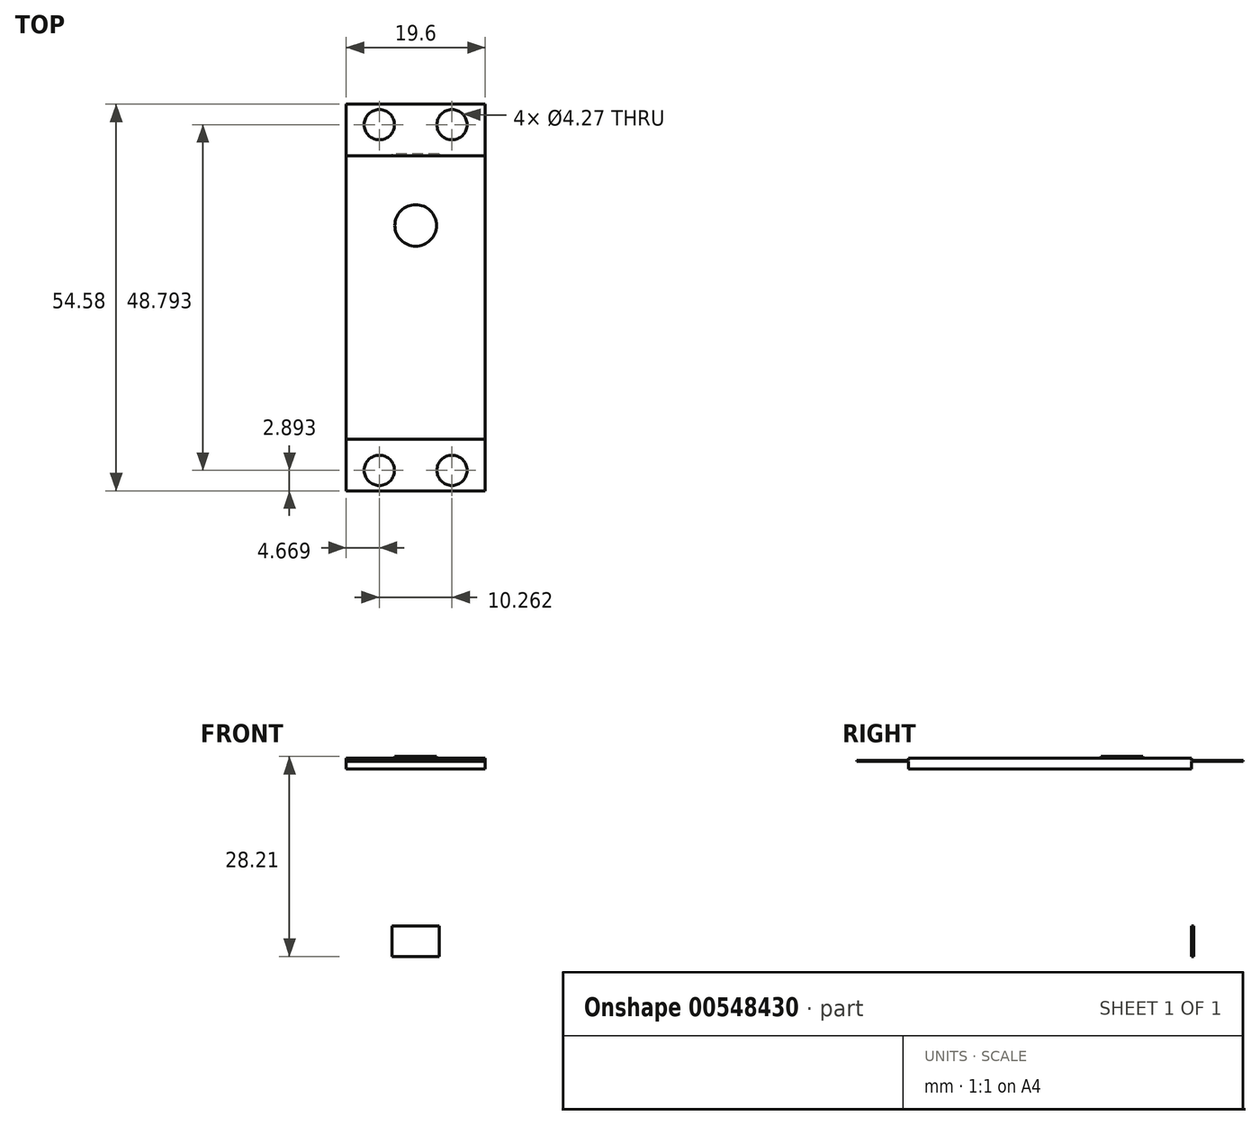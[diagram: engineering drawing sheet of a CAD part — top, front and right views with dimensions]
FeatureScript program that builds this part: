
annotation { "Feature Type Name" : "Feature", "Feature Type Description" : "" }
export const myFeature = defineFeature(function(context is Context, id is Id, definition is map)
    precondition{}
    {
        {
            assignVariable(context, id + "F0", {"name" : "EarDepth", "anyValue" : .3250});
        }
        {
            assignVariable(context, id + "F1", {"name" : "EarThick", "anyValue" : .137});
        }
        {
            assignVariable(context, id + "F2", {"name" : "ServoL", "anyValue" : 1.54});
        }
        {
            assignVariable(context, id + "F3", {"name" : "ServoAxleL", "anyValue" : 0.23});
        }
        {
            var Q0;
            Q0=qCreatedBy(makeId("Top.planeOp"),FACE);
            var sketch = newSketch(context, id + "F4", { "sketchPlane" : qUnion([Q0])});
            skLineSegment(sketch, "E0.bottom", {"start": v(-9.8, -27.3) * mm, "end": v(9.8, -27.3) * mm});
            skLineSegment(sketch, "E0.top", {"start": v(-9.8, 27.3) * mm, "end": v(9.8, 27.3) * mm});
            skLineSegment(sketch, "E0.left", {"start": v(-9.8, -27.3) * mm, "end": v(-9.8, 27.3) * mm});
            skLineSegment(sketch, "E0.right", {"start": v(9.8, -27.3) * mm, "end": v(9.8, 27.3) * mm});
            skPoint(sketch, "E0.middle", {"position": v(0, 0) * mm});
            skLineSegment(sketch, "E1", {"start": v(-9.8, 19.98) * mm, "end": v(9.8, 19.98) * mm});
            skLineSegment(sketch, "E2", {"start": v(-9.8, -19.98) * mm, "end": v(9.8, -19.98) * mm});
            skCircle(sketch, "E3", {"center": v(0, 10.17) * mm, "radius": 2.93 * mm});
            skCircle(sketch, "E4", {"center": v(5.13, 24.4) * mm, "radius": 2.13 * mm});
            skCircle(sketch, "E5.MirrorC", {"center": v(-5.13, 24.4) * mm, "radius": 2.13 * mm});
            skCircle(sketch, "E6.MirrorC", {"center": v(-5.13, -24.4) * mm, "radius": 2.13 * mm});
            skCircle(sketch, "E7.MirrorC", {"center": v(5.13, -24.4) * mm, "radius": 2.13 * mm});
            skSolve(sketch);
        }
        {
            var Q0;
            Q0=makeQuery(id+"F4.imprint","IMPRINT",FACE,{"disambiguationData":[TD([[makeQuery(id+"F4.imprint","IMPRINT",EDGE,{"derivedFrom":sQuery(id+"F4.wireOp",EDGE,"E3")}),1.0]])]});
            extrude(context, id + "F5", {"entities" : qUnion([Q0]), "depth" : (getVariable(context, 'ServoAxleL') + getVariable(context, 'EarDepth')) * mm, "offsetDistance" : 25.4 * mm});
        }
        {
            var Q0;
            {var subQ1=sQuery(id+"F4.wireOp",EDGE,"E1");Q0=makeQuery(id+"F4.imprint","IMPRINT",FACE,{"disambiguationData":[TD([[makeQuery(id+"F4.imprint","IMPRINT",EDGE,{"derivedFrom":subQ1}),-1.0]])]});}
            var Q1;
            Q1=makeQuery(id+"F4.imprint","IMPRINT",FACE,{"disambiguationData":[TD([[makeQuery(id+"F4.imprint","IMPRINT",EDGE,{"derivedFrom":sQuery(id+"F4.wireOp",EDGE,"E3")}),1.0]])]});
            extrude(context, id + "F6", {"entities" : qUnion([Q0, Q1]), "operationType" : NewBodyOperationType.ADD, "depth" : (getVariable(context, 'EarDepth')) * mm, "offsetDistance" : 25.4 * mm, "hasSecondDirection" : true, "secondDirectionOppositeDirection" : true, "secondDirectionDepth" : (getVariable(context, 'ServoL') - getVariable(context, 'EarDepth')) * mm});
        }
        {
            var Q0;
            {var subQ2=sQuery(id+"F4.wireOp",EDGE,"E0.top");Q0=makeQuery(id+"F4.imprint","IMPRINT",FACE,{"disambiguationData":[TD([[makeQuery(id+"F4.imprint","IMPRINT",EDGE,{"derivedFrom":subQ2}),-1.0]])]});}
            var Q1;
            {var subQ2=sQuery(id+"F4.wireOp",EDGE,"E0.bottom");Q1=makeQuery(id+"F4.imprint","IMPRINT",FACE,{"disambiguationData":[TD([[makeQuery(id+"F4.imprint","IMPRINT",EDGE,{"derivedFrom":subQ2}),1.0]])]});}
            extrude(context, id + "F7", {"entities" : qUnion([Q0, Q1]), "operationType" : NewBodyOperationType.ADD, "oppositeDirection" : true, "depth" : (getVariable(context, 'EarThick')) * mm, "offsetDistance" : 25.4 * mm});
        }
        {
            assignVariable(context, id + "F8", {"name" : "WireH", "anyValue" : .3});
        }
        {
            var Q0;
            {var subQ0=sQuery(id+"F4.wireOp",EDGE,"E1");var subQ1=sQuery(id+"F4.wireOp",EDGE,"E0.right");var subQ2=sQuery(id+"F4.wireOp",EDGE,"E0.left");var subQ5=sQuery(id+"F4.wireOp",EDGE,"E2");Q0=makeQuery(id+"F7.boolean.opBoolean","SPLIT",FACE,{"disambiguationData":[TD([makeQuery(id+"F6.opExtrude","CAP_FACE",FACE,{"disambiguationData":[OSD([subQ2,subQ1,subQ0,subQ5])],"isStart":true})])],"derivedFrom":makeQuery(id+"F6.opExtrude","SWEPT_FACE",FACE,{"disambiguationData":[OSD([subQ0])]})});}
            var sketch = newSketch(context, id + "F9", { "sketchPlane" : qUnion([Q0])});
            skLineSegment(sketch, "E8.bottom", {"start": v(-3.33, -27.66) * mm, "end": v(3.33, -27.66) * mm});
            skLineSegment(sketch, "E8.top", {"start": v(-3.33, -23.34) * mm, "end": v(3.33, -23.34) * mm});
            skLineSegment(sketch, "E8.left", {"start": v(-3.33, -27.66) * mm, "end": v(-3.33, -23.34) * mm});
            skLineSegment(sketch, "E8.right", {"start": v(3.33, -27.66) * mm, "end": v(3.33, -23.34) * mm});
            skPoint(sketch, "E8.middle", {"position": v(0, -25.5) * mm});
            skPoint(sketch, "E8.middle.positionSnap0", {"position": v(0, -30.96) * mm});
            skPoint(sketch, "E8.centerSnap0", {"position": v(0, -30.96) * mm});
            skSolve(sketch);
        }
        {
            var Q0;
            Q0=makeQuery(id+"F9.imprint","IMPRINT",FACE,{"disambiguationData":[TD([[makeQuery(id+"F9.imprint","IMPRINT",EDGE,{"derivedFrom":sQuery(id+"F9.wireOp",EDGE,"E8.bottom")}),1.0]])]});
            extrude(context, id + "F10", {"entities" : qUnion([Q0]), "operationType" : NewBodyOperationType.ADD, "depth" : (getVariable(context, 'WireH')) * mm, "offsetDistance" : 25.4 * mm});
        }
    });
